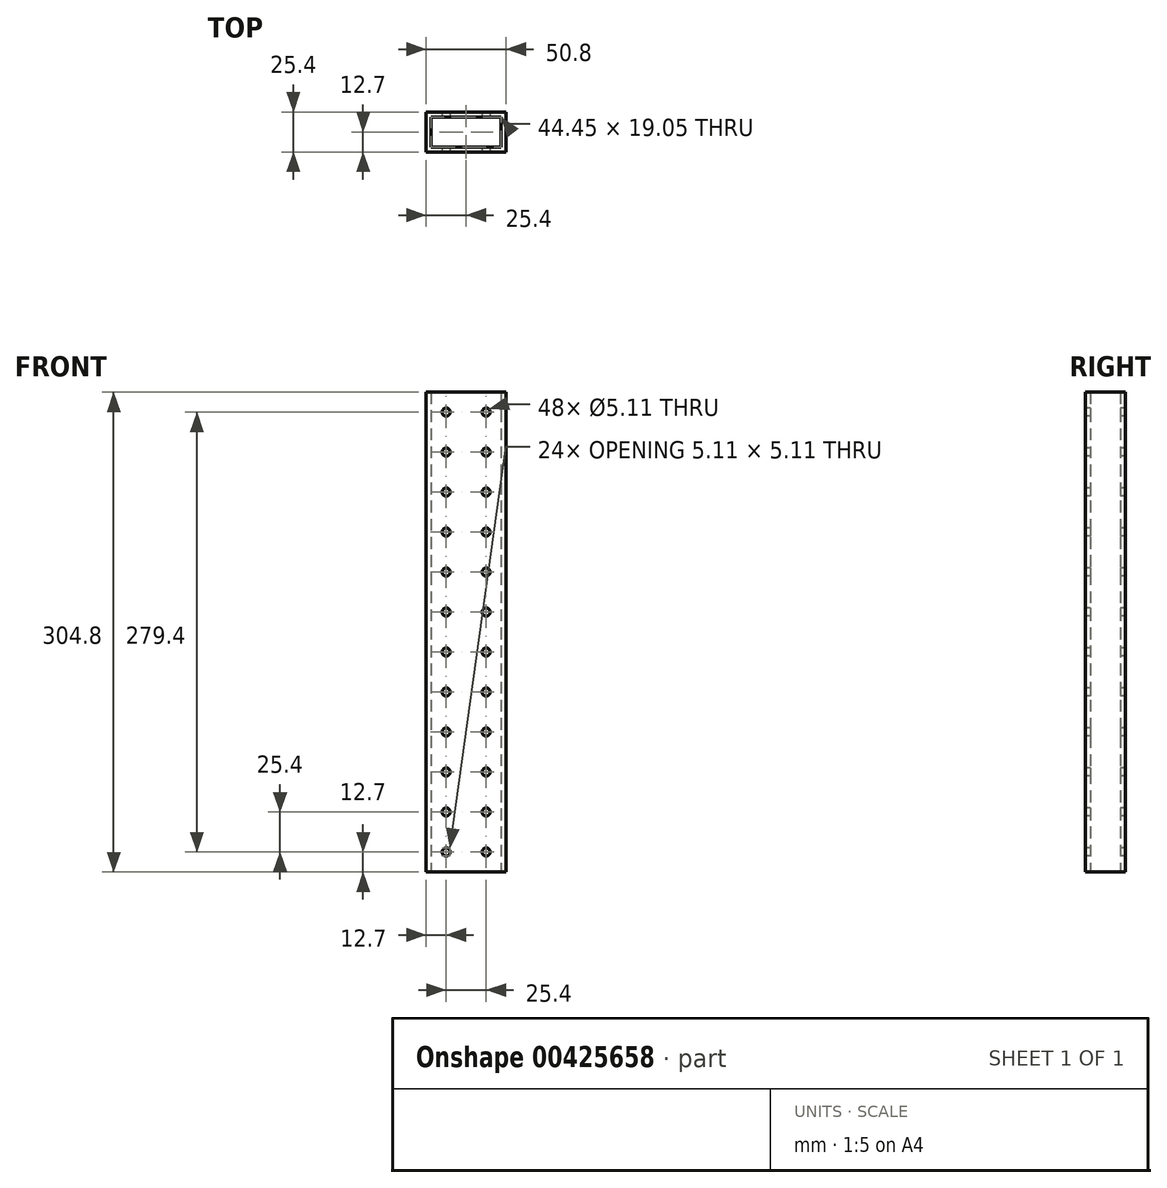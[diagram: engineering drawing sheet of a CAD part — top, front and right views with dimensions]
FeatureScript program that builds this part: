
annotation { "Feature Type Name" : "Feature", "Feature Type Description" : "" }
export const myFeature = defineFeature(function(context is Context, id is Id, definition is map)
    precondition{}
    {
        {
            var Q0;
            Q0=qCreatedBy(makeId("Top.planeOp"),FACE);
            var sketch = newSketch(context, id + "F0", { "sketchPlane" : qUnion([Q0])});
            skLineSegment(sketch, "E0.bottom", {"start": v(-25.4, 12.7) * mm, "end": v(25.4, 12.7) * mm});
            skLineSegment(sketch, "E0.top", {"start": v(-25.4, -12.7) * mm, "end": v(25.4, -12.7) * mm});
            skLineSegment(sketch, "E0.left", {"start": v(-25.4, 12.7) * mm, "end": v(-25.4, -12.7) * mm});
            skLineSegment(sketch, "E0.right", {"start": v(25.4, 12.7) * mm, "end": v(25.4, -12.7) * mm});
            skPoint(sketch, "E0.middle", {"position": v(0, 0) * mm});
            skLineSegment(sketch, "E1.bottom", {"start": v(-22.23, 9.53) * mm, "end": v(22.23, 9.53) * mm});
            skLineSegment(sketch, "E1.top", {"start": v(-22.23, -9.53) * mm, "end": v(22.23, -9.53) * mm});
            skLineSegment(sketch, "E1.left", {"start": v(-22.23, 9.53) * mm, "end": v(-22.23, -9.53) * mm});
            skLineSegment(sketch, "E1.right", {"start": v(22.23, 9.53) * mm, "end": v(22.23, -9.53) * mm});
            skSolve(sketch);
        }
        {
            var Q0;
            Q0=makeQuery(id+"F0.imprint","IMPRINT",FACE,{"disambiguationData":[TD([[makeQuery(id+"F0.imprint","IMPRINT",EDGE,{"derivedFrom":sQuery(id+"F0.wireOp",EDGE,"E0.bottom")}),-1.0]])]});
            extrude(context, id + "F1", {"entities" : qUnion([Q0]), "depth" : 304.8 * mm, "offsetDistance" : 25.4 * mm});
        }
        {
            var Q0;
            Q0=makeQuery(id+"F1.opExtrude","SWEPT_FACE",FACE,{"disambiguationData":[OSD([sQuery(id+"F0.wireOp",EDGE,"E0.top")])]});
            var sketch = newSketch(context, id + "F2", { "sketchPlane" : qUnion([Q0])});
            skCircle(sketch, "E2", {"center": v(-12.7, 292.1) * mm, "radius": 2.55 * mm});
            skCircle(sketch, "E3.0.1.0", {"center": v(-12.7, 266.7) * mm, "radius": 2.55 * mm});
            skCircle(sketch, "E3.0.2.0", {"center": v(-12.7, 241.3) * mm, "radius": 2.55 * mm});
            skCircle(sketch, "E3.0.3.0", {"center": v(-12.7, 215.9) * mm, "radius": 2.55 * mm});
            skCircle(sketch, "E3.0.4.0", {"center": v(-12.7, 190.5) * mm, "radius": 2.55 * mm});
            skCircle(sketch, "E3.0.5.0", {"center": v(-12.7, 165.1) * mm, "radius": 2.55 * mm});
            skCircle(sketch, "E3.0.6.0", {"center": v(-12.7, 139.7) * mm, "radius": 2.55 * mm});
            skCircle(sketch, "E3.0.7.0", {"center": v(-12.7, 114.3) * mm, "radius": 2.55 * mm});
            skCircle(sketch, "E3.0.8.0", {"center": v(-12.7, 88.9) * mm, "radius": 2.55 * mm});
            skCircle(sketch, "E3.0.9.0", {"center": v(-12.7, 63.5) * mm, "radius": 2.55 * mm});
            skCircle(sketch, "E3.0.10.0", {"center": v(-12.7, 38.1) * mm, "radius": 2.55 * mm});
            skCircle(sketch, "E3.0.11.0", {"center": v(-12.7, 12.7) * mm, "radius": 2.55 * mm});
            skCircle(sketch, "E3.1.0.0", {"center": v(12.7, 292.1) * mm, "radius": 2.55 * mm});
            skCircle(sketch, "E3.1.1.0", {"center": v(12.7, 266.7) * mm, "radius": 2.55 * mm});
            skCircle(sketch, "E3.1.2.0", {"center": v(12.7, 241.3) * mm, "radius": 2.55 * mm});
            skCircle(sketch, "E3.1.3.0", {"center": v(12.7, 215.9) * mm, "radius": 2.55 * mm});
            skCircle(sketch, "E3.1.4.0", {"center": v(12.7, 190.5) * mm, "radius": 2.55 * mm});
            skCircle(sketch, "E3.1.5.0", {"center": v(12.7, 165.1) * mm, "radius": 2.55 * mm});
            skCircle(sketch, "E3.1.6.0", {"center": v(12.7, 139.7) * mm, "radius": 2.55 * mm});
            skCircle(sketch, "E3.1.7.0", {"center": v(12.7, 114.3) * mm, "radius": 2.55 * mm});
            skCircle(sketch, "E3.1.8.0", {"center": v(12.7, 88.9) * mm, "radius": 2.55 * mm});
            skCircle(sketch, "E3.1.9.0", {"center": v(12.7, 63.5) * mm, "radius": 2.55 * mm});
            skCircle(sketch, "E3.1.10.0", {"center": v(12.7, 38.1) * mm, "radius": 2.55 * mm});
            skCircle(sketch, "E3.1.11.0", {"center": v(12.7, 12.7) * mm, "radius": 2.55 * mm});
            skLineSegment(sketch, "E3.direction1", {"start": v(-12.7, 292.1) * mm, "end": v(12.7, 292.1) * mm, "construction": true});
            skLineSegment(sketch, "E3.direction2", {"start": v(-12.7, 292.1) * mm, "end": v(-12.7, 266.7) * mm, "construction": true});
            skSolve(sketch);
        }
        {
            var Q0;
            Q0 = qSketchRegion(id + "F2", true);
            extrude(context, id + "F3", {"entities" : qUnion([Q0]), "operationType" : NewBodyOperationType.REMOVE, "oppositeDirection" : true, "depth" : 25.4 * mm, "offsetDistance" : 25.4 * mm});
        }
    });
